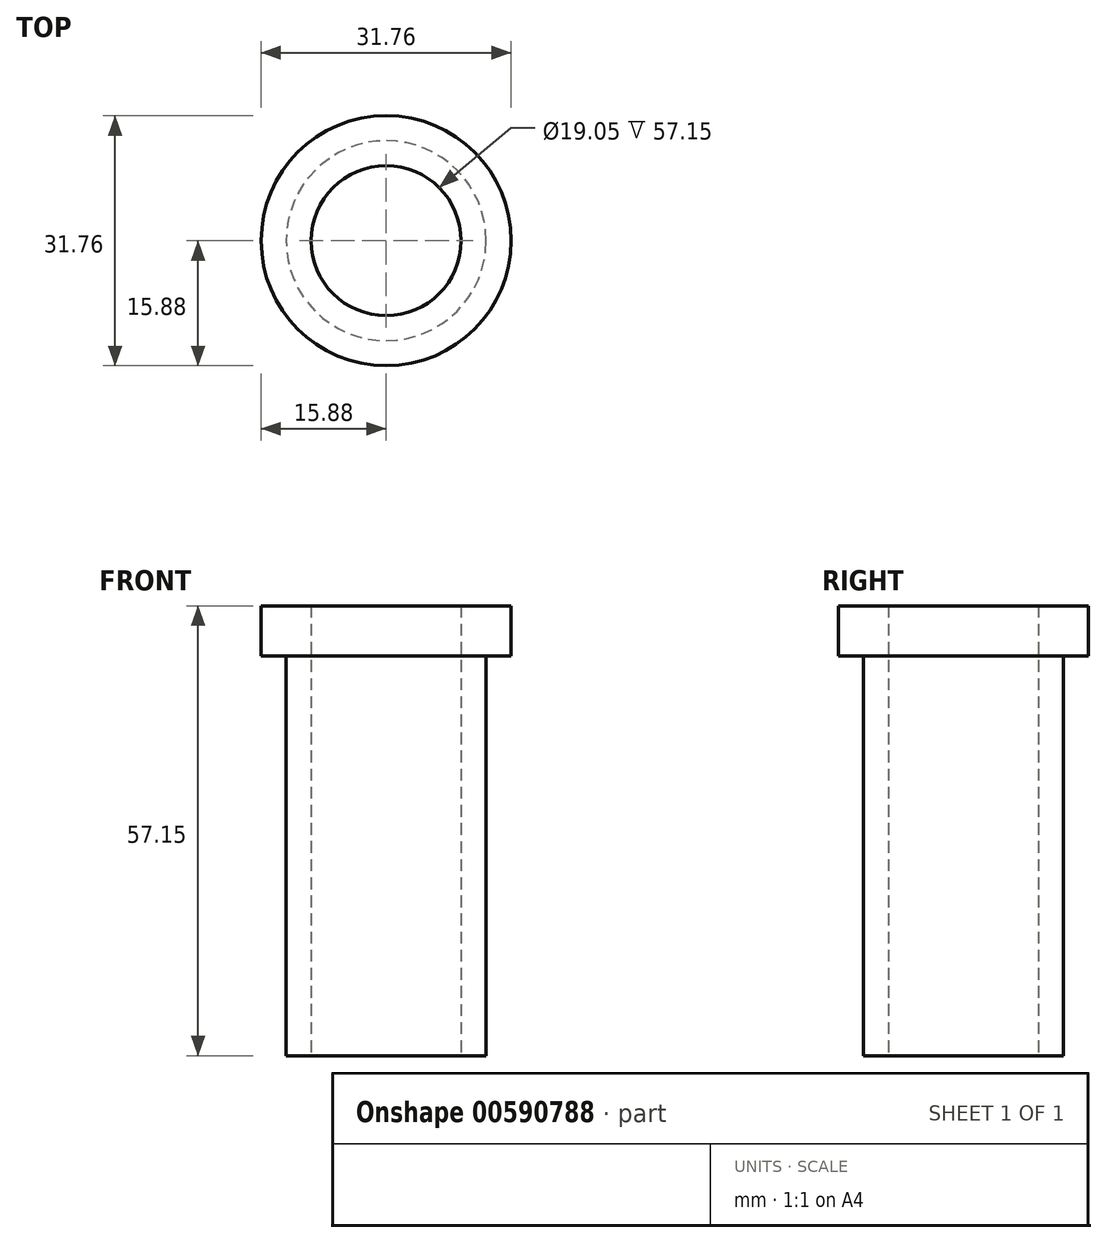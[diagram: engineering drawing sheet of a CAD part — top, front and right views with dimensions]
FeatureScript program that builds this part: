
annotation { "Feature Type Name" : "Feature", "Feature Type Description" : "" }
export const myFeature = defineFeature(function(context is Context, id is Id, definition is map)
    precondition{}
    {
        {
            var Q0;
            Q0=qCreatedBy(makeId("Top.planeOp"),FACE);
            var sketch = newSketch(context, id + "F0", { "sketchPlane" : qUnion([Q0])});
            skCircle(sketch, "E0", {"center": v(0, 0) * mm, "radius": 15.88 * mm});
            skCircle(sketch, "E1", {"center": v(0, 0) * mm, "radius": 9.53 * mm});
            skSolve(sketch);
        }
        {
            var Q0;
            Q0 = qSketchRegion(id + "F0", true);
            extrude(context, id + "F1", {"entities" : qUnion([Q0]), "depth" : 57.15 * mm, "offsetDistance" : 25.4 * mm});
        }
        {
            var Q0;
            Q0=makeQuery(id+"F1.opExtrude","CAP_FACE",FACE,{"disambiguationData":[OSD([sQuery(id+"F0.wireOp",EDGE,"E0"),sQuery(id+"F0.wireOp",EDGE,"E1")])],"isStart":true});
            var sketch = newSketch(context, id + "F2", { "sketchPlane" : qUnion([Q0])});
            skCircle(sketch, "E2", {"center": v(0, 0) * mm, "radius": 12.7 * mm});
            skCircle(sketch, "E3", {"center": v(0, 0) * mm, "radius": 22.36 * mm});
            skSolve(sketch);
        }
        {
            var Q0;
            Q0 = qSketchRegion(id + "F2", true);
            extrude(context, id + "F3", {"entities" : qUnion([Q0]), "operationType" : NewBodyOperationType.REMOVE, "oppositeDirection" : true, "depth" : 50.8 * mm, "offsetDistance" : 25.4 * mm});
        }
    });
